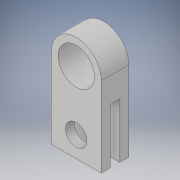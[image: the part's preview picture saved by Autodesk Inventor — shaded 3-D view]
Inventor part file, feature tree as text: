
AUTODESK INVENTOR PART (.ipt)
format: ipt  version: 2019 (Build 230136000, 136)  size: 142,848 bytes
history: native  units: in
note: dims shown in document units (in); Inventor stores cm internally (conversion verified against a paired STEP export)
features: sketch x4, extrude x2, hole x1
ambient origin geometry x8: Origin, YZ Plane, XZ Plane, XY Plane, X Axis, Y Axis, Z Axis, Center Point
bodies: Body1 (feature_tree)
feature tree (7):
  extrude  "Extrusion2"  Depth=0.25in
  hole  "Hole1"  [1 undecoded]
  extrude  "Extrusion3"  Depth=0.35in
  sketch  "Sketch7"  dims[d19=0.325in d20=2.0in d21=0.0in d23=2.0in d24=0.75in d25=2.16in]
  sketch  "Sketch1"  dims[d0=1.32in d1=0.25in]
  sketch  "Sketch3"  dims[d7=1.0in d8=0.0in]
  sketch  "Sketch6"  dims[d9=0.781in d10=0.75in d11=1.125in d12=0.364in d13=0.5635in d14=1.0in d15=0.8108in d18=0.35in]
note: 1 required parameter value undecoded (feature->parameter linkage not recoverable at this tier; creation-order binding heuristic only, values carry confidence <= 0.55)
